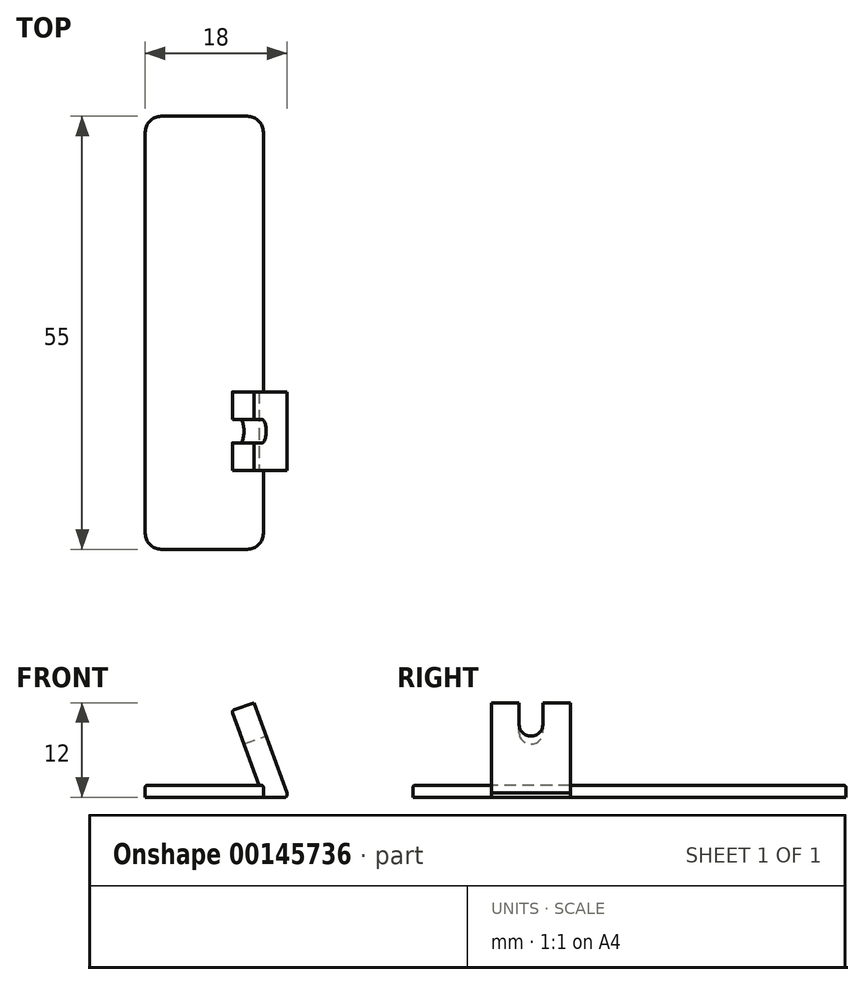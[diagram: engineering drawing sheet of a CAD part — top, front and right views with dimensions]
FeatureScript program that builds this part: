
annotation { "Feature Type Name" : "Feature", "Feature Type Description" : "" }
export const myFeature = defineFeature(function(context is Context, id is Id, definition is map)
    precondition{}
    {
        {
            var Q0;
            Q0=qCreatedBy(makeId("Top.planeOp"),FACE);
            var sketch = newSketch(context, id + "F0", { "sketchPlane" : qUnion([Q0])});
            skLineSegment(sketch, "E0.bottom", {"start": v(-6.58, 27.5) * mm, "end": v(8.42, 27.5) * mm});
            skLineSegment(sketch, "E0.top", {"start": v(-6.58, -27.5) * mm, "end": v(8.42, -27.5) * mm});
            skLineSegment(sketch, "E0.left", {"start": v(-6.58, 27.5) * mm, "end": v(-6.58, -27.5) * mm});
            skLineSegment(sketch, "E0.right", {"start": v(8.42, 27.5) * mm, "end": v(8.42, -27.5) * mm});
            skPoint(sketch, "E0.middle", {"position": v(0.92, 0) * mm});
            skLineSegment(sketch, "E1", {"start": v(-34.15, 0) * mm, "end": v(31.64, 0) * mm, "construction": true});
            skPoint(sketch, "E1.startSnap0", {"position": v(-6.58, 0) * mm});
            skLineSegment(sketch, "E2.bottom", {"start": v(8.42, -7.5) * mm, "end": v(11.42, -7.5) * mm});
            skLineSegment(sketch, "E2.top", {"start": v(8.42, -17.5) * mm, "end": v(11.42, -17.5) * mm});
            skLineSegment(sketch, "E2.left", {"start": v(8.42, -7.5) * mm, "end": v(8.42, -17.5) * mm, "construction": true});
            skLineSegment(sketch, "E2.right", {"start": v(11.42, -7.5) * mm, "end": v(11.42, -17.5) * mm});
            skLineSegment(sketch, "E3", {"start": v(8.42, -12.5) * mm, "end": v(11.42, -12.5) * mm, "construction": true});
            skLineSegment(sketch, "E4", {"start": v(8.42, -17.5) * mm, "end": v(-1.58, -17.5) * mm});
            skLineSegment(sketch, "E5", {"start": v(8.42, -7.5) * mm, "end": v(-1.58, -7.5) * mm});
            skLineSegment(sketch, "E6", {"start": v(-1.58, -7.5) * mm, "end": v(-1.58, -17.5) * mm});
            skSolve(sketch);
        }
        {
            var Q0;
            {var subQ1=sQuery(id+"F0.wireOp",EDGE,"E0.bottom");Q0=makeQuery(id+"F0.imprint","IMPRINT",FACE,{"disambiguationData":[TD([[makeQuery(id+"F0.imprint","IMPRINT",EDGE,{"derivedFrom":subQ1}),-1.0]])]});}
            extrude(context, id + "F1", {"entities" : qUnion([Q0]), "depth" : 1.5 * mm});
        }
        {
            var Q0;
            {var subQ0=sQuery(id+"F0.wireOp",EDGE,"E2.bottom");Q0=makeQuery(id+"F0.imprint","IMPRINT",FACE,{"disambiguationData":[TD([[makeQuery(id+"F0.imprint","IMPRINT",EDGE,{"derivedFrom":subQ0}),-1.0]])]});}
            var Q1;
            {var subQ2=sQuery(id+"F0.wireOp",EDGE,"E4");Q1=makeQuery(id+"F0.imprint","IMPRINT",FACE,{"disambiguationData":[TD([[makeQuery(id+"F0.imprint","IMPRINT",EDGE,{"derivedFrom":subQ2}),-1.0]])]});}
            extrude(context, id + "F2", {"entities" : qUnion([Q0, Q1]), "operationType" : NewBodyOperationType.ADD, "depth" : 12 * mm});
        }
        {
            var Q0;
            Q0=makeQuery(id+"F2.opExtrude","SWEPT_FACE",FACE,{"disambiguationData":[OSD([sQuery(id+"F0.wireOp",EDGE,"E2.top")])]});
            var sketch = newSketch(context, id + "F3", { "sketchPlane" : qUnion([Q0])});
            skSolve(sketch);
        }
        {
            var Q0;
            Q0=makeQuery(id+"F1.opExtrude","SWEPT_EDGE",EDGE,{"disambiguationData":[OSD([sQuery(id+"F0.wireOp",EDGE,"E0.top"),sQuery(id+"F0.wireOp",EDGE,"E0.left")])]});
            var Q1;
            Q1=makeQuery(id+"F1.opExtrude","SWEPT_EDGE",EDGE,{"disambiguationData":[OSD([sQuery(id+"F0.wireOp",EDGE,"E0.top"),sQuery(id+"F0.wireOp",EDGE,"E0.right")])]});
            var Q2;
            Q2=makeQuery(id+"F1.opExtrude","SWEPT_EDGE",EDGE,{"disambiguationData":[OSD([sQuery(id+"F0.wireOp",EDGE,"E0.bottom"),sQuery(id+"F0.wireOp",EDGE,"E0.left")])]});
            var Q3;
            Q3=makeQuery(id+"F1.opExtrude","SWEPT_EDGE",EDGE,{"disambiguationData":[OSD([sQuery(id+"F0.wireOp",EDGE,"E0.bottom"),sQuery(id+"F0.wireOp",EDGE,"E0.right")])]});
            var Q4;
            Q4=makeQuery(id+"FampwR42kzeWOgi_1.boolean.opBoolean","INTERSECT",EDGE,{"derivedFrom":[makeQuery(id+"F2.opExtrude","SWEPT_FACE",FACE,{"disambiguationData":[OSD([sQuery(id+"F0.wireOp",EDGE,"E2.bottom")])]}),makeQuery(id+"FampwR42kzeWOgi_1.opExtrude","SWEPT_FACE",FACE,{"disambiguationData":[OSD([sQuery(id+"F3.wireOp",EDGE,"44b091da-c608-4ac1-a8e1-9d7b321e9dd7")])]})]});
            var Q5;
            Q5=makeQuery(id+"FampwR42kzeWOgi_1.boolean.opBoolean","COPY",EDGE,{"derivedFrom":makeQuery(id+"FampwR42kzeWOgi_1.opExtrude","CAP_EDGE",EDGE,{"disambiguationData":[OSD([sQuery(id+"F3.wireOp",EDGE,"44b091da-c608-4ac1-a8e1-9d7b321e9dd7")])],"isStart":true})});
            fillet(context, id + "F4", {"entities" : qUnion([Q0, Q1, Q2, Q3, Q4, Q5]), "radius" : 2 * mm, "tangentPropagation" : true, "allowEdgeOverflow" : false});
        }
        {
            var Q0;
            {var subQ1=sQuery(id+"F0.wireOp",EDGE,"E2.top");Q0=makeQuery(id+"F3.imprint","IMPRINT",FACE,{"disambiguationData":[TD([[makeQuery(id+"F3.imprint","IMPRINT",EDGE,{"derivedFrom":makeQuery(id+"F2.opExtrude","CAP_EDGE",EDGE,{"disambiguationData":[OSD([subQ1])],"isStart":true})}),1.0]])]});}
            var sketch = newSketch(context, id + "F5", { "sketchPlane" : qUnion([Q0])});
            skLineSegment(sketch, "E7.0", {"start": v(11.42, 12) * mm, "end": v(11.42, 0) * mm});
            skLineSegment(sketch, "E8.0", {"start": v(-1.58, 12) * mm, "end": v(11.42, 12) * mm});
            skLineSegment(sketch, "E9.0", {"start": v(-1.58, 12) * mm, "end": v(-1.58, 1.5) * mm});
            skLineSegment(sketch, "E10.0", {"start": v(-4.58, 1.5) * mm, "end": v(6.42, 1.5) * mm});
            skLineSegment(sketch, "E11.0", {"start": v(6.42, 1.5) * mm, "end": v(8.42, 1.5) * mm});
            skLineSegment(sketch, "E12.0", {"start": v(8.42, 1.5) * mm, "end": v(8.42, 0) * mm});
            skLineSegment(sketch, "E13.0", {"start": v(8.42, 0) * mm, "end": v(11.42, 0) * mm});
            skLineSegment(sketch, "E14", {"start": v(11.42, 0.53) * mm, "end": v(7.25, 12) * mm});
            skLineSegment(sketch, "E15.0", {"start": v(8.42, 0) * mm, "end": v(4.05, 12) * mm});
            skLineSegment(sketch, "E16", {"start": v(7.25, 12) * mm, "end": v(4.43, 10.97) * mm});
            skSolve(sketch);
        }
        {
            var Q0;
            {var subQ3=sQuery(id+"F5.wireOp",EDGE,"E14");Q0=makeQuery(id+"F5.imprint","IMPRINT",FACE,{"disambiguationData":[TD([[makeQuery(id+"F5.imprint","IMPRINT",EDGE,{"derivedFrom":subQ3}),-1.0]])]});}
            var Q1;
            {var subQ5=sQuery(id+"F5.wireOp",EDGE,"E9.0");Q1=makeQuery(id+"F5.imprint","IMPRINT",FACE,{"disambiguationData":[TD([[makeQuery(id+"F5.imprint","IMPRINT",EDGE,{"derivedFrom":subQ5}),1.0]])]});}
            var Q2;
            {var subQ0=sQuery(id+"F5.wireOp",EDGE,"E16");Q2=makeQuery(id+"F5.imprint","IMPRINT",FACE,{"disambiguationData":[TD([[makeQuery(id+"F5.imprint","IMPRINT",EDGE,{"derivedFrom":subQ0}),-1.0]])]});}
            extrude(context, id + "F6", {"entities" : qUnion([Q0, Q1, Q2]), "operationType" : NewBodyOperationType.REMOVE, "oppositeDirection" : true, "depth" : 25 * mm});
        }
        {
            var Q0;
            Q0=makeQuery(id+"F6.boolean.opBoolean","COPY",FACE,{"derivedFrom":makeQuery(id+"F6.opExtrude","SWEPT_FACE",FACE,{"disambiguationData":[OSD([sQuery(id+"F5.wireOp",EDGE,"E14")])]})});
            var sketch = newSketch(context, id + "F7", { "sketchPlane" : qUnion([Q0])});
            skCircle(sketch, "E17", {"center": v(-12.5, 5.8) * mm, "radius": 1.5 * mm});
            skPoint(sketch, "E17.centerSnap0", {"position": v(-17.5, 5.8) * mm});
            skLineSegment(sketch, "E18", {"start": v(-11, 5.8) * mm, "end": v(-11, 8.8) * mm});
            skLineSegment(sketch, "E19", {"start": v(-14, 5.8) * mm, "end": v(-14, 8.8) * mm});
            skSolve(sketch);
        }
        {
            var Q0;
            {var subQ0=sQuery(id+"F5.wireOp",EDGE,"E14");var subQ1=sQuery(id+"F5.wireOp",EDGE,"E8.0");var subQ2=sQuery(id+"F5.wireOp",EDGE,"E16");Q0=makeQuery(id+"F6.boolean.opBoolean","TWEAK_EDGE",EDGE,{"disambiguationData":[OD(0.0)],"derivedFrom":[makeQuery(id+"F6.opExtrude","SWEPT_EDGE",EDGE,{"disambiguationData":[OSD([subQ1,subQ0,subQ2]),ownerDisambiguation([makeQuery(id+"F6.opExtrude","SWEPT_BODY",BODY,{"disambiguationData":[OSD([subQ1,sQuery(id+"F5.wireOp",EDGE,"E9.0"),sQuery(id+"F5.wireOp",EDGE,"E10.0"),sQuery(id+"F5.wireOp",EDGE,"E11.0"),sQuery(id+"F5.wireOp",EDGE,"E15.0"),subQ2])]})])]}),makeQuery(id+"F6.opExtrude","SWEPT_EDGE",EDGE,{"disambiguationData":[OSD([subQ1,subQ0,subQ2]),ownerDisambiguation([makeQuery(id+"F6.opExtrude","SWEPT_BODY",BODY,{"disambiguationData":[OSD([sQuery(id+"F5.wireOp",EDGE,"E7.0"),subQ1,subQ0])]})])]})]});}
            var Q1;
            {var subQ0=sQuery(id+"F5.wireOp",EDGE,"E14");var subQ1=sQuery(id+"F5.wireOp",EDGE,"E8.0");var subQ2=sQuery(id+"F5.wireOp",EDGE,"E16");Q1=makeQuery(id+"F6.boolean.opBoolean","TWEAK_EDGE",EDGE,{"disambiguationData":[OD(1.0)],"derivedFrom":[makeQuery(id+"F6.opExtrude","SWEPT_EDGE",EDGE,{"disambiguationData":[OSD([subQ1,subQ0,subQ2]),ownerDisambiguation([makeQuery(id+"F6.opExtrude","SWEPT_BODY",BODY,{"disambiguationData":[OSD([subQ1,sQuery(id+"F5.wireOp",EDGE,"E9.0"),sQuery(id+"F5.wireOp",EDGE,"E10.0"),sQuery(id+"F5.wireOp",EDGE,"E11.0"),sQuery(id+"F5.wireOp",EDGE,"E15.0"),subQ2])]})])]}),makeQuery(id+"F6.opExtrude","SWEPT_EDGE",EDGE,{"disambiguationData":[OSD([subQ1,subQ0,subQ2]),ownerDisambiguation([makeQuery(id+"F6.opExtrude","SWEPT_BODY",BODY,{"disambiguationData":[OSD([sQuery(id+"F5.wireOp",EDGE,"E7.0"),subQ1,subQ0])]})])]})]});}
            var Q2;
            {var subQ0=sQuery(id+"F5.wireOp",EDGE,"E15.0");var subQ1=sQuery(id+"F5.wireOp",EDGE,"E16");Q2=makeQuery(id+"F6.boolean.opBoolean","COPY",EDGE,{"disambiguationData":[TD([makeQuery(id+"FAERSWvBysWDfgc_1.boolean.opBoolean","COPY",FACE,{"derivedFrom":makeQuery(id+"FAERSWvBysWDfgc_1.opExtrude","SWEPT_FACE",FACE,{"disambiguationData":[OSD([sQuery(id+"F7.wireOp",EDGE,"E19")])]})})])],"derivedFrom":makeQuery(id+"F6.opExtrude","SWEPT_EDGE",EDGE,{"disambiguationData":[OSD([subQ0,subQ1])]})});}
            var Q3;
            {var subQ0=sQuery(id+"F5.wireOp",EDGE,"E15.0");var subQ1=sQuery(id+"F5.wireOp",EDGE,"E16");Q3=makeQuery(id+"F6.boolean.opBoolean","COPY",EDGE,{"disambiguationData":[TD([makeQuery(id+"FAERSWvBysWDfgc_1.boolean.opBoolean","COPY",FACE,{"derivedFrom":makeQuery(id+"FAERSWvBysWDfgc_1.opExtrude","SWEPT_FACE",FACE,{"disambiguationData":[OSD([sQuery(id+"F7.wireOp",EDGE,"E18")])]})})])],"derivedFrom":makeQuery(id+"F6.opExtrude","SWEPT_EDGE",EDGE,{"disambiguationData":[OSD([subQ0,subQ1])]})});}
            var Q4;
            Q4=makeQuery(id+"F6.boolean.opBoolean","COPY",EDGE,{"derivedFrom":makeQuery(id+"F6.opExtrude","SWEPT_EDGE",EDGE,{"disambiguationData":[OSD([sQuery(id+"F5.wireOp",EDGE,"E7.0"),sQuery(id+"F5.wireOp",EDGE,"E14")])]})});
            var Q5;
            Q5=makeQuery(id+"F2.opExtrude","CAP_EDGE",EDGE,{"disambiguationData":[OSD([sQuery(id+"F0.wireOp",EDGE,"E2.right")])],"isStart":true});
            var Q6;
            {var subQ0=sQuery(id+"F0.wireOp",EDGE,"E0.right");Q6=makeQuery(id+"F1.opExtrude","CAP_EDGE",EDGE,{"disambiguationData":[OSD([subQ0]),TDD([makeQuery(id+"F0.imprint","IMPRINT",EDGE,{"disambiguationData":[TD([[makeQuery(id+"F0.imprint","INTERSECT",VERTEX,{"derivedFrom":[sQuery(id+"F0.wireOp",EDGE,"E0.top"),subQ0]}),1.0]])],"derivedFrom":subQ0})])],"isStart":false});}
            var Q7;
            {var subQ0=sQuery(id+"F0.wireOp",EDGE,"E0.right");Q7=makeQuery(id+"F1.opExtrude","CAP_EDGE",EDGE,{"disambiguationData":[OSD([subQ0]),TDD([makeQuery(id+"F0.imprint","IMPRINT",EDGE,{"disambiguationData":[TD([[makeQuery(id+"F0.imprint","INTERSECT",VERTEX,{"derivedFrom":[sQuery(id+"F0.wireOp",EDGE,"E0.bottom"),subQ0]}),-1.0]])],"derivedFrom":subQ0})])],"isStart":false});}
            fillet(context, id + "F8", {"entities" : qUnion([Q0, Q1, Q2, Q3, Q4, Q5, Q6, Q7]), "radius" : .25 * mm, "tangentPropagation" : true, "allowEdgeOverflow" : false});
        }
        {
            var Q0;
            {var subQ0=sQuery(id+"F7.wireOp",EDGE,"E17");var subQ1=makeQuery(id+"F7.imprint","INTERSECT",VERTEX,{"derivedFrom":[subQ0,sQuery(id+"F7.wireOp",EDGE,"E18")]});Q0=makeQuery(id+"F7.imprint","IMPRINT",FACE,{"disambiguationData":[TD([[makeQuery(id+"F7.imprint","IMPRINT",EDGE,{"disambiguationData":[TD([[subQ1,-1.0]])],"derivedFrom":subQ0}),1.0]])]});}
            var Q1;
            {var subQ0=sQuery(id+"F7.wireOp",EDGE,"E18");Q1=makeQuery(id+"F7.imprint","IMPRINT",FACE,{"disambiguationData":[TD([[makeQuery(id+"F7.imprint","IMPRINT",EDGE,{"derivedFrom":subQ0}),1.0]])]});}
            extrude(context, id + "F9", {"entities" : qUnion([Q0, Q1]), "operationType" : NewBodyOperationType.REMOVE, "oppositeDirection" : true, "depth" : 25 * mm});
        }
    });
